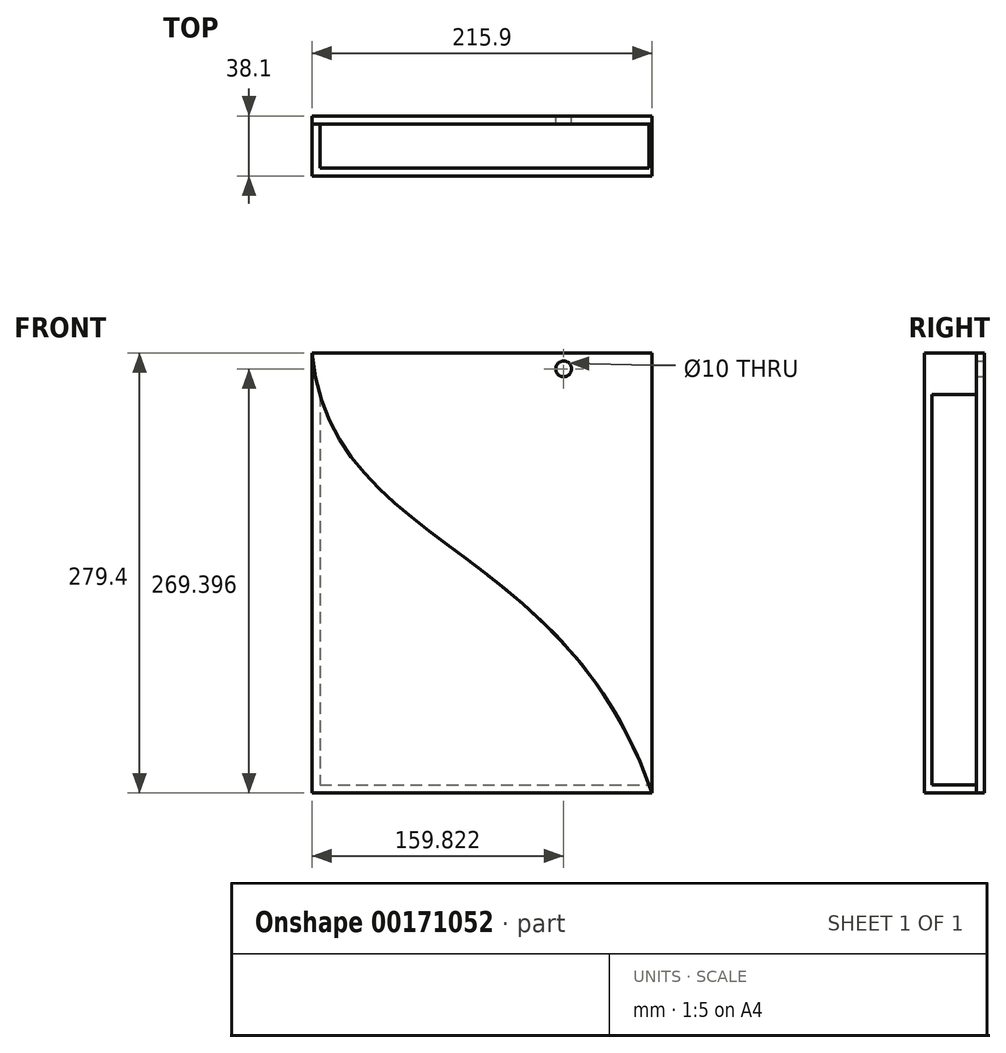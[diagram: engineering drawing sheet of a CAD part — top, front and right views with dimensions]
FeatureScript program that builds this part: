
annotation { "Feature Type Name" : "Feature", "Feature Type Description" : "" }
export const myFeature = defineFeature(function(context is Context, id is Id, definition is map)
    precondition{}
    {
        {
            var Q0;
            Q0=qCreatedBy(makeId("Front.planeOp"),FACE);
            var sketch = newSketch(context, id + "F0", { "sketchPlane" : qUnion([Q0])});
            skLineSegment(sketch, "E0.bottom", {"start": v(-84.91, 181.9) * mm, "end": v(130.99, 181.9) * mm});
            skLineSegment(sketch, "E0.top", {"start": v(-84.91, -97.5) * mm, "end": v(130.99, -97.5) * mm});
            skLineSegment(sketch, "E0.left", {"start": v(-84.91, 181.9) * mm, "end": v(-84.91, -97.5) * mm});
            skLineSegment(sketch, "E0.right", {"start": v(130.99, 181.9) * mm, "end": v(130.99, -97.5) * mm});
            skPoint(sketch, "E0.middle", {"position": v(23.04, 42.2) * mm});
            skFitSpline(sketch, "E1", {"points": [v(-84.91, 181.9) * mm, v(130.99, -97.5) * mm], "startDerivative": vector(36.37, -375.41) * mm, "endDerivative": vector(166.43, -484.3) * mm});
            skSolve(sketch);
        }
        {
            var Q0;
            Q0=makeQuery(id+"F0.imprint","IMPRINT",FACE,{"disambiguationData":[TD([[makeQuery(id+"F0.imprint","IMPRINT",EDGE,{"derivedFrom":sQuery(id+"F0.wireOp",EDGE,"E0.top")}),1.0]])]});
            extrude(context, id + "F1", {"entities" : qUnion([Q0]), "depth" : 38.1 * mm});
        }
        {
            var Q0;
            Q0=makeQuery(id+"F0.imprint","IMPRINT",FACE,{"disambiguationData":[TD([[makeQuery(id+"F0.imprint","IMPRINT",EDGE,{"derivedFrom":sQuery(id+"F0.wireOp",EDGE,"E0.bottom")}),-1.0]])]});
            extrude(context, id + "F2", {"entities" : qUnion([Q0]), "operationType" : NewBodyOperationType.ADD, "depth" : 5 * mm});
        }
        {
            var Q0;
            Q0=makeQuery(id+"F1.opExtrude","SWEPT_FACE",FACE,{"disambiguationData":[OSD([sQuery(id+"F0.wireOp",EDGE,"E1")])]});
            shell(context, id + "F3", {"entities" : qUnion([Q0]), "thickness" : 5 * mm});
        }
        {
            var Q0;
            {var subQ0=sQuery(id+"F0.wireOp",EDGE,"E1");var subQ1=sQuery(id+"F0.wireOp",EDGE,"E0.right");var subQ2=sQuery(id+"F0.wireOp",EDGE,"E0.bottom");Q0=makeQuery(id+"F3.opShell","MERGE",FACE,{"derivedFrom":[makeQuery(id+"F2.opExtrude","CAP_FACE",FACE,{"disambiguationData":[OSD([subQ2,subQ1,subQ0])],"isStart":false}),makeQuery(id+"F2.boolean.opBoolean","MERGE",FACE,{"derivedFrom":[makeQuery(id+"F1.opExtrude","CAP_FACE",FACE,{"disambiguationData":[OSD([sQuery(id+"F0.wireOp",EDGE,"E0.top"),sQuery(id+"F0.wireOp",EDGE,"E0.left"),subQ0])],"isStart":true}),makeQuery(id+"F2.opExtrude","CAP_FACE",FACE,{"disambiguationData":[OSD([subQ2,subQ1,subQ0])],"isStart":true})]})]});}
            var sketch = newSketch(context, id + "F4", { "sketchPlane" : qUnion([Q0])});
            skCircle(sketch, "E2", {"center": v(120.99, 171.9) * mm, "radius": 5 * mm});
            skCircle(sketch, "E3", {"center": v(-74.91, 171.9) * mm, "radius": 5 * mm});
            skSolve(sketch);
        }
        {
            var Q0;
            Q0=makeQuery(id+"F4.imprint","IMPRINT",FACE,{"disambiguationData":[TD([[makeQuery(id+"F4.imprint","IMPRINT",EDGE,{"derivedFrom":sQuery(id+"F4.wireOp",EDGE,"E3")}),1.0]])]});
            var Q1;
            Q1=makeQuery(id+"F4.imprint","IMPRINT",FACE,{"disambiguationData":[TD([[makeQuery(id+"F4.imprint","IMPRINT",EDGE,{"derivedFrom":sQuery(id+"F4.wireOp",EDGE,"E2")}),1.0]])]});
            extrude(context, id + "F5", {"entities" : qUnion([Q0, Q1]), "operationType" : NewBodyOperationType.REMOVE, "oppositeDirection" : true, "depth" : 5 * mm});
        }
        {
            var Q0;
            Q0=qCreatedBy(makeId("Right.planeOp"),FACE);
            var sketch = newSketch(context, id + "F6", { "sketchPlane" : qUnion([Q0])});
            skLineSegment(sketch, "E4.bottom", {"start": v(-33.1, 42.2) * mm, "end": v(-5, 42.2) * mm});
            skLineSegment(sketch, "E4.top", {"start": v(-33.1, -92.5) * mm, "end": v(-5, -92.5) * mm});
            skLineSegment(sketch, "E4.left", {"start": v(-33.1, 42.2) * mm, "end": v(-33.1, -92.5) * mm});
            skLineSegment(sketch, "E4.right", {"start": v(-5, 42.2) * mm, "end": v(-5, -92.5) * mm});
            skSolve(sketch);
        }
        {
            var Q0;
            Q0=qSketchRegion(id+"F6",true);
            extrude(context, id + "F7", {"entities" : qUnion([Q0]), "operationType" : NewBodyOperationType.REMOVE, "depth" : 152.4 * mm});
        }
    });
